# Revit family: 6L-WS-D
name_source: partatom
category: Lighting Fixtures
units: mm (PartAtom-declared; Revit-internal decimal feet)

## family parameters
Cut with Voids When Loaded = No
Host = Face
Light Source = Yes
OmniClass Number = 23.80.70.11.14.17
OmniClass Title = Direct/Indirect
Part Type = Normal
Room Calculation Point = No
Round Connector Dimension = Use Diameter
Shared = Yes

## types (1)
- 6L-WS-D-4-SOF
    Apparent Load = 0 VA
    Application = Commercial Indoor,Institutional,Retail,Education,Healthcare,Library,Office,Perimeter Lighting,Public Space
    Assembly Code = D5020200
    Bulb = Glass  - White
    Circuiting = 1Circuit
    Color Filter = 16777215
    Default Elevation = 48 "
    Depth = 4.315 "
    Description = MOD™ 6 LED Perimeter Wall/Slot® Direct
    Dimming Lamp Color Temperature Shift = <None>
    Emit Shape Visible in Rendering = No
    Emit from Rectangle Length = 5.75 "
    Emit from Rectangle Width = 47 "
    Ending Length = 24 "
    Features = Variable Intensity technology provides specifiable
lumen output/wattage
• End cap design eliminates visible diffuser seams/gaps
• 2 SDCM color variation
    Fixture Distribution = Direct/Asymmetric Direct
    Glass = Paint - Textured Matte White
    Height = 10.5 "
    Housing Material = Paint -  Matte White
    Lamp = LED
    Load Classification = Lighting
    Manufacturer = Litecontrol
    Model = MOD™ 6 LED Perimeter Wall/Slot® Direct
    Mounting = Perimeter
    Photometric Notes = More IES files download on Photometric Link
    Photometric Web File = 6L-WSx-D-4-SOF-X-CX-35K-D035.ies
    Power Factor = 1
    Row Length = 48 "
    Starting Length = -24 "
    Tilt Angle = 90.00°
    Type Comments = Lighting Fixture
    URL = https://www.currentlighting.com
    Voltage = 120 V
    Warranty = 5-Years Warranty
    Wattage Comments = 18W
    Width = 6.75 "

## geometry (parser evidence)
native form markers: Sweep x2
no freeform markers — native parametric forms only
